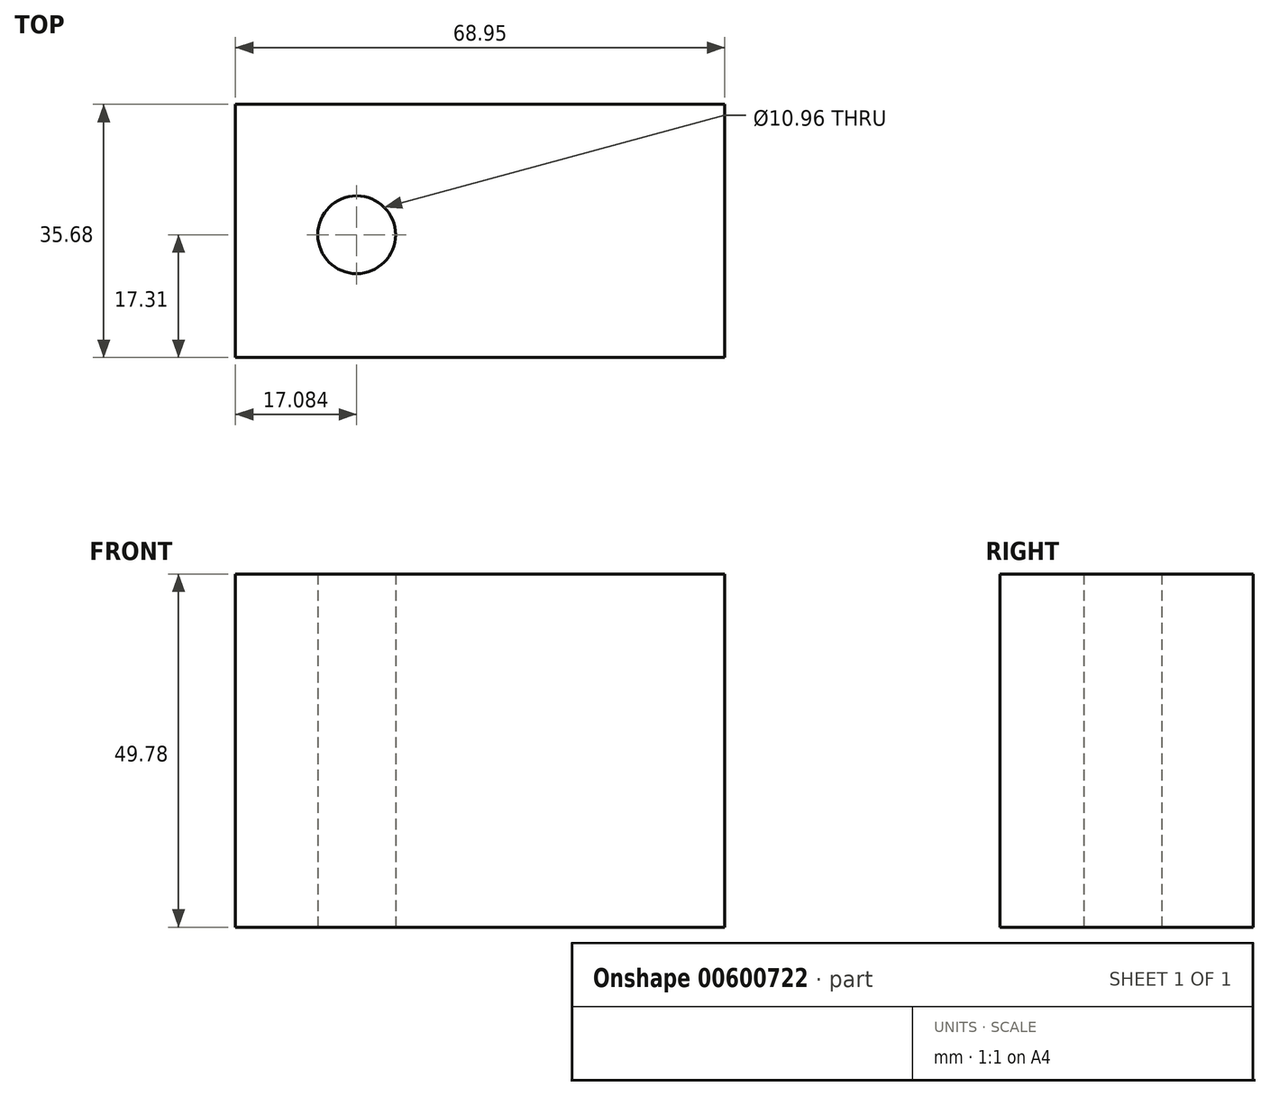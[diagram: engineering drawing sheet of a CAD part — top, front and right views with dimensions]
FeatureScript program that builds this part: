
annotation { "Feature Type Name" : "Feature", "Feature Type Description" : "" }
export const myFeature = defineFeature(function(context is Context, id is Id, definition is map)
    precondition{}
    {
        {
            var Q0;
            Q0=qCreatedBy(makeId("Top.planeOp"),FACE);
            var sketch = newSketch(context, id + "F0", { "sketchPlane" : qUnion([Q0])});
            skLineSegment(sketch, "E0.bottom", {"start": v(-35.3, 18.37) * mm, "end": v(33.65, 18.37) * mm});
            skLineSegment(sketch, "E0.top", {"start": v(-35.3, -17.3) * mm, "end": v(33.65, -17.3) * mm});
            skLineSegment(sketch, "E0.left", {"start": v(-35.3, 18.37) * mm, "end": v(-35.3, -17.3) * mm});
            skLineSegment(sketch, "E0.right", {"start": v(33.65, 18.37) * mm, "end": v(33.65, -17.3) * mm});
            skCircle(sketch, "E1", {"center": v(-18.22, 0) * mm, "radius": 5.48 * mm});
            skSolve(sketch);
        }
        {
            var Q0;
            Q0 = qSketchRegion(id + "F0", true);
            extrude(context, id + "F1", {"entities" : qUnion([Q0]), "depth" : 49.78 * mm, "offsetDistance" : 25.4 * mm});
        }
    });
